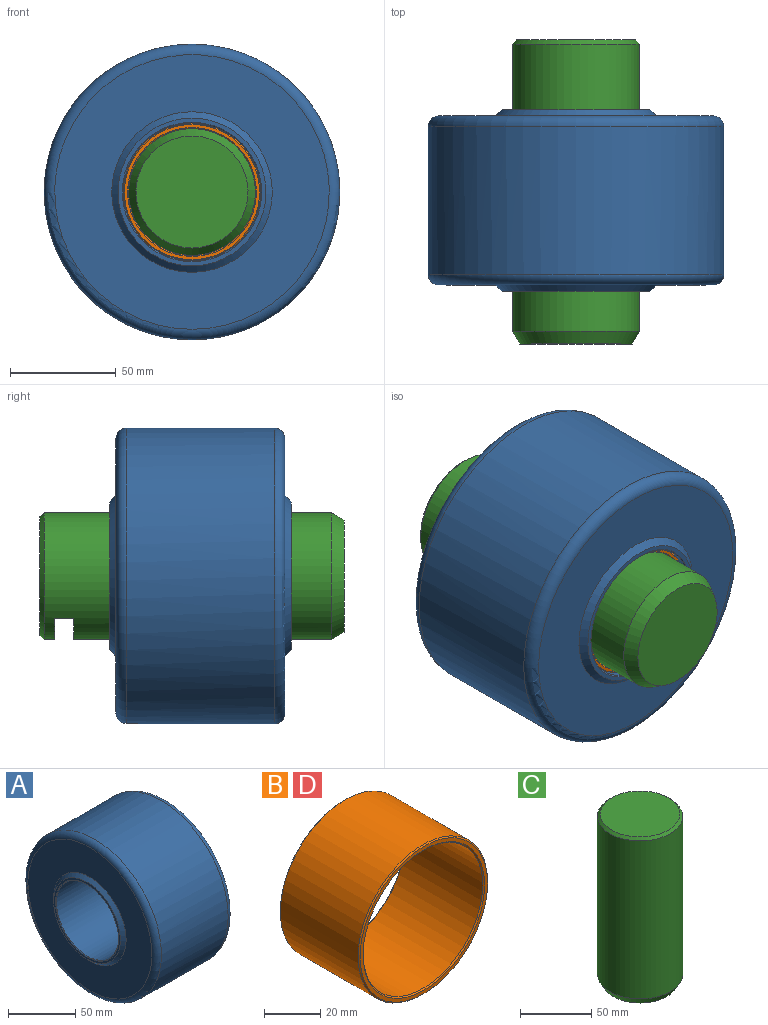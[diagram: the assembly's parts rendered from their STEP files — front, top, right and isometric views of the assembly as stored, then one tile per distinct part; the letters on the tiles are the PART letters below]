
ASSEMBLY  parts=4 mates=6
PART A: 12 faces, bbox 86x151.5x151.5 mm
  f0: cone r=38mm half-angle=45deg, axis (1,0,0), area 973mm2, adj f1,f7
  f1: plane 70x70mm, normal (-1,0,0), area 427.3mm2, adj f0,f11
  f2: cylinder r=32.5mm len=85mm, axis (-1,0,0), area 17357.3mm2, adj f10,f11
  f3: plane 70x70mm, normal (1,0,0), area 427.3mm2, adj f4,f10
  f4: cone r=35mm half-angle=45deg, axis (-1,0,0), area 973mm2, adj f3,f5
  f5: plane 130x130mm, normal (1,0,0), area 8736.8mm2, adj f4,f8
  f6: cylinder r=70mm len=140mm, axis (-1,0,0), area 30787.6mm2, adj f8,f9
  f7: plane 130x130mm, normal (-1,0,0), area 8736.8mm2, adj f0,f9
  f8: torus R=65mm, axis (-1,0,0), area 3364.7mm2, adj f5,f6
  f9: torus R=65mm, axis (1,0,0), area 3364.7mm2, adj f6,f7
  f10: cone r=33mm half-angle=45deg, axis (1,0,0), area 145.5mm2, adj f2,f3
  f11: cone r=32.5mm half-angle=45deg, axis (-1,0,0), area 145.5mm2, adj f1,f2
PART B: 8 faces, bbox 65x40x65 mm
  f0: cylinder r=30mm len=60mm, axis (0,1,0), area 7351.3mm2, adj f6,f7
  f1: cylinder r=32.5mm len=65mm, axis (0,1,0), area 7963.9mm2, adj f4,f5
  f2: plane 64x64mm, normal (0,-1,0), area 294.5mm2, adj f4,f6
  f3: plane 64x64mm, normal (0,1,0), area 294.5mm2, adj f5,f7
  f4: cone r=32mm half-angle=45deg, axis (0,1,0), area 143.3mm2, adj f1,f2
  f5: cone r=32.5mm half-angle=45deg, axis (0,-1,0), area 143.3mm2, adj f1,f3
  f6: cone r=30mm half-angle=45deg, axis (0,-1,0), area 134.4mm2, adj f0,f2
  f7: cone r=30.5mm half-angle=45deg, axis (0,1,0), area 134.4mm2, adj f0,f3
PART C: 8 faces, bbox 60x60x144 mm
  f0: cylinder r=30mm len=136mm, axis (0,0,-1), area 25181.2mm2, adj f3,f4,f5,f6,f7
  f1: plane 56x56mm, normal (0,0,1), area 2463mm2, adj f3
  f2: plane 53.07x53.07mm, normal (0,0,-1), area 2212.2mm2, adj f4
  f3: cone r=28mm half-angle=45deg, axis (0,0,-1), area 515.4mm2, adj f0,f1
  f4: cone r=30mm half-angle=30deg, axis (0,0,1), area 1230.5mm2, adj f0,f2
  f5: plane 44.72x9mm, normal (1,0,0), area 402.5mm2, adj f0,f6,f7
  f6: plane 44.72x10mm, normal (0,0,1), area 309.7mm2, adj f0,f5
  f7: plane 44.72x10mm, normal (0,0,-1), area 309.7mm2, adj f0,f5
PART D: same geometry as B
PLACE A rot(axis=(0,0,1),90deg) t=(0,-40,0)mm
PLACE B t=(0,-60,0)mm
PLACE C rot(axis=(-0.58,0.58,0.58),120deg) t=(0,-36,0)mm
PLACE D t=(0,-20,0)mm
MATE planar C.f6 <-> A.f0  axis (0,1,0) through (0,20,-24.06)mm
MATE slider A.f0 <-> C.f0  axis (0,-1,0) through (0,-40,0)mm
MATE planar B.f0 <-> A.f0  axis (0,-1,0) through (0,-80,0)mm
MATE planar D.f0 <-> A.f0  axis (0,1,0) through (0,0,0)mm
MATE slider B.f0 <-> A.f0  axis (0,1,0) through (0,-60,0)mm
MATE slider D.f0 <-> A.f0  axis (0,1,0) through (0,-39.5,0)mm
